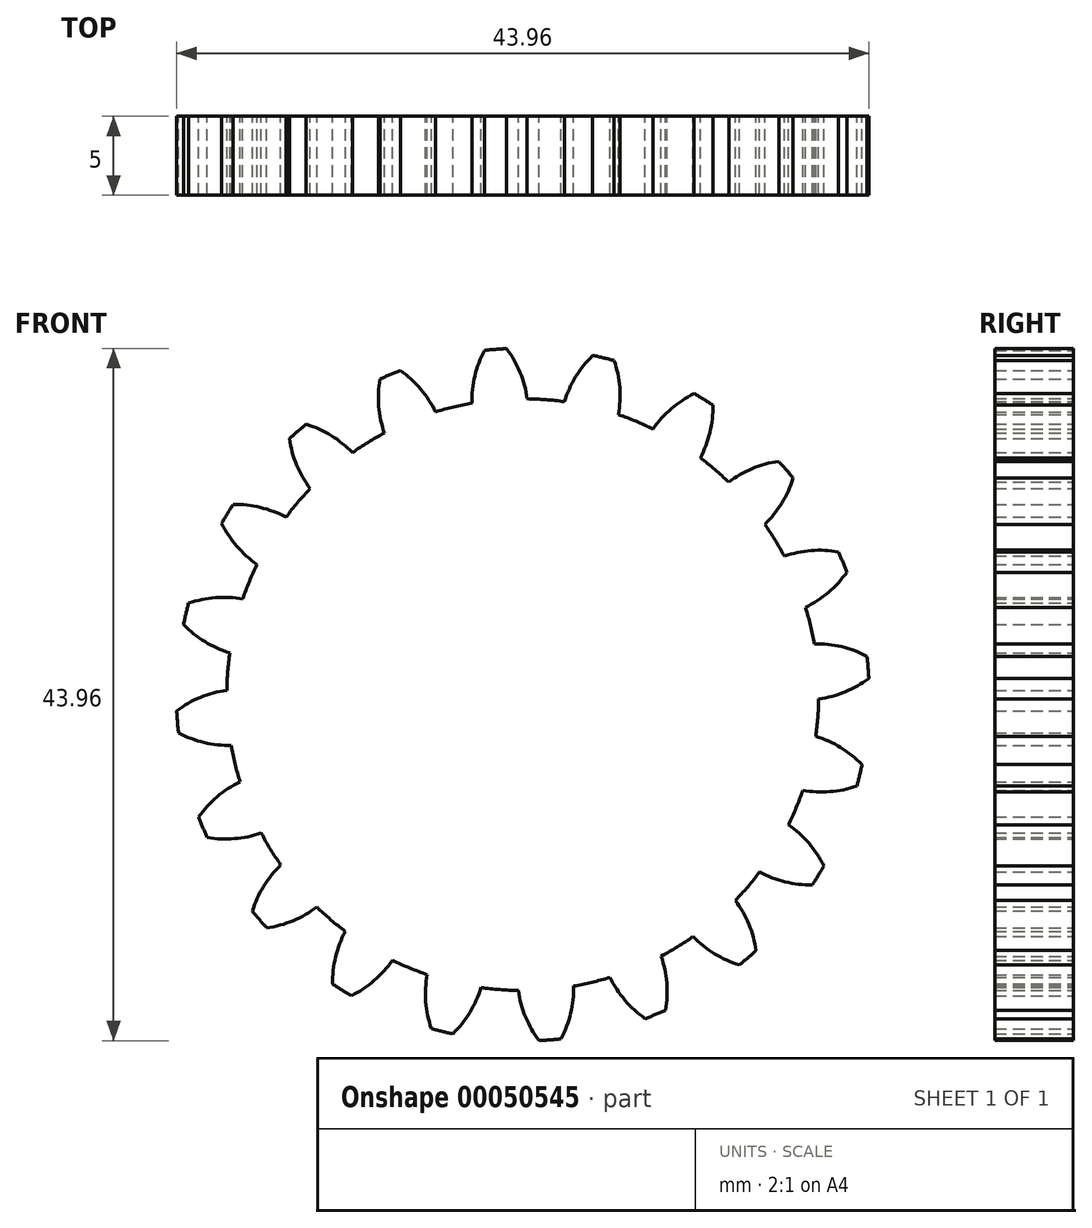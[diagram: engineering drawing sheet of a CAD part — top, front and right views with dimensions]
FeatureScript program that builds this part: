
annotation { "Feature Type Name" : "Feature", "Feature Type Description" : "" }
export const myFeature = defineFeature(function(context is Context, id is Id, definition is map)
    precondition{}
    {
        {
            assignVariable(context, id + "F0", {"name" : "teeth", "anyValue" : 20});
        }
        {
            var Q0;
            Q0=qCreatedBy(makeId("Front.planeOp"),FACE);
            var sketch = newSketch(context, id + "F1", { "sketchPlane" : qUnion([Q0])});
            skCircle(sketch, "E0", {"center": v(0, 0) * mm, "radius": 20 * mm, "construction": true});
            skCircle(sketch, "E1", {"center": v(0, 0) * mm, "radius": 22 * mm, "construction": true});
            skCircle(sketch, "E2", {"center": v(0, 0) * mm, "radius": 18.8 * mm});
            skCircle(sketch, "E3", {"center": v(40, 0) * mm, "radius": 18.8 * mm, "construction": true});
            skLineSegment(sketch, "E4", {"start": v(17.66, 6.43) * mm, "end": v(20, 0) * mm, "construction": true});
            skLineSegment(sketch, "E5", {"start": v(0, 0) * mm, "end": v(20, 0) * mm, "construction": true});
            skLineSegment(sketch, "E6", {"start": v(20, 0) * mm, "end": v(20, 28.46) * mm, "construction": true});
            skLineSegment(sketch, "E7", {"start": v(20, 0) * mm, "end": v(22.34, -6.43) * mm, "construction": true});
            skLineSegment(sketch, "E8", {"start": v(20, 0) * mm, "end": v(40, 0) * mm, "construction": true});
            skLineSegment(sketch, "E9", {"start": v(17.66, 6.43) * mm, "end": v(0, 0) * mm, "construction": true});
            skArc(sketch, "E10", {"start": v(17.66, 6.43) * mm, "mid": v(18.53, 3.13) * mm, "end": v(18.8, -0.28) * mm, "construction": true});
            skArc(sketch, "E11", {"start": v(18.8, -0.28) * mm, "mid": v(18.01, 5.36) * mm, "end": v(15.58, 10.51) * mm, "construction": true});
            skLineSegment(sketch, "E12", {"start": v(15.58, 10.51) * mm, "end": v(0, 0) * mm, "construction": true});
            skLineSegment(sketch, "E13", {"start": v(15.58, 10.51) * mm, "end": v(21.98, 1.03) * mm, "construction": true});
            skLineSegment(sketch, "E14", {"start": v(18.8, -0.28) * mm, "end": v(0, 0) * mm, "construction": true});
            skArc(sketch, "E15", {"start": v(18.8, -0.28) * mm, "mid": v(20.47, 0.17) * mm, "end": v(21.98, 1.03) * mm});
            skLineSegment(sketch, "E16", {"start": v(0, 0) * mm, "end": v(21.93, 1.73) * mm, "construction": true});
            skArc(sketch, "E17.MirrorCS", {"start": v(18.51, 3.23) * mm, "mid": v(20.24, 3.04) * mm, "end": v(21.87, 2.43) * mm});
            skPoint(sketch, "E18", {"position": v(19.75, 3.14) * mm});
            skArc(sketch, "E19", {"start": v(21.98, 1.03) * mm, "mid": v(21.93, 1.73) * mm, "end": v(21.87, 2.43) * mm});
            skPoint(sketch, "E20", {"position": v(18.74, 1.48) * mm});
            skArc(sketch, "E21", {"start": v(18.8, -0.28) * mm, "mid": v(18.74, 1.48) * mm, "end": v(18.51, 3.23) * mm});
            skSolve(sketch);
        }
        {
            var Q0;
            {var subQ0=sQuery(id+"F1.wireOp",EDGE,"E2");var subQ1=makeQuery(id+"F1.imprint","INTERSECT",VERTEX,{"derivedFrom":[subQ0,sQuery(id+"F1.wireOp",EDGE,"E15")]});Q0=makeQuery(id+"F1.imprint","IMPRINT",FACE,{"disambiguationData":[TD([[makeQuery(id+"F1.imprint","IMPRINT",EDGE,{"disambiguationData":[TD([[subQ1,1.0]])],"derivedFrom":subQ0}),1.0]])]});}
            extrude(context, id + "F2", {"entities" : qUnion([Q0]), "depth" : 5 * mm});
        }
        {
            var Q0;
            {var subQ0=sQuery(id+"F1.wireOp",EDGE,"E15");Q0=makeQuery(id+"F1.imprint","IMPRINT",FACE,{"disambiguationData":[TD([[makeQuery(id+"F1.imprint","IMPRINT",EDGE,{"derivedFrom":subQ0}),1.0]])]});}
            extrude(context, id + "F3", {"entities" : qUnion([Q0]), "depth" : 5 * mm});
        }
        {
            var Q0;
            Q0=qCreatedBy(makeId("Right.planeOp"),FACE);
            var sketch = newSketch(context, id + "F4", { "sketchPlane" : qUnion([Q0])});
            skLineSegment(sketch, "E22", {"start": v(0, 0) * mm, "end": v(12.3, 0) * mm});
            skSolve(sketch);
        }
        {
            var Q0;
            Q0=makeQuery(id+"F3.opExtrude","SWEPT_BODY",BODY,{"disambiguationData":[OSD([sQuery(id+"F1.wireOp",EDGE,"E2"),sQuery(id+"F1.wireOp",EDGE,"E15"),sQuery(id+"F1.wireOp",EDGE,"E17.MirrorCS"),sQuery(id+"F1.wireOp",EDGE,"E19")])]});
            var Q1;
            Q1=sQuery(id+"F4.wireOp",EDGE,"E22");
            circularPattern(context, id + "F5", {"operationType" : NewBodyOperationType.ADD, "entities" : qUnion([Q0]), "axis" : qUnion([Q1]), "angle" : (360 / getVariable(context, 'teeth')) * degree, "instanceCount" : getVariable(context, 'teeth')});
        }
    });
